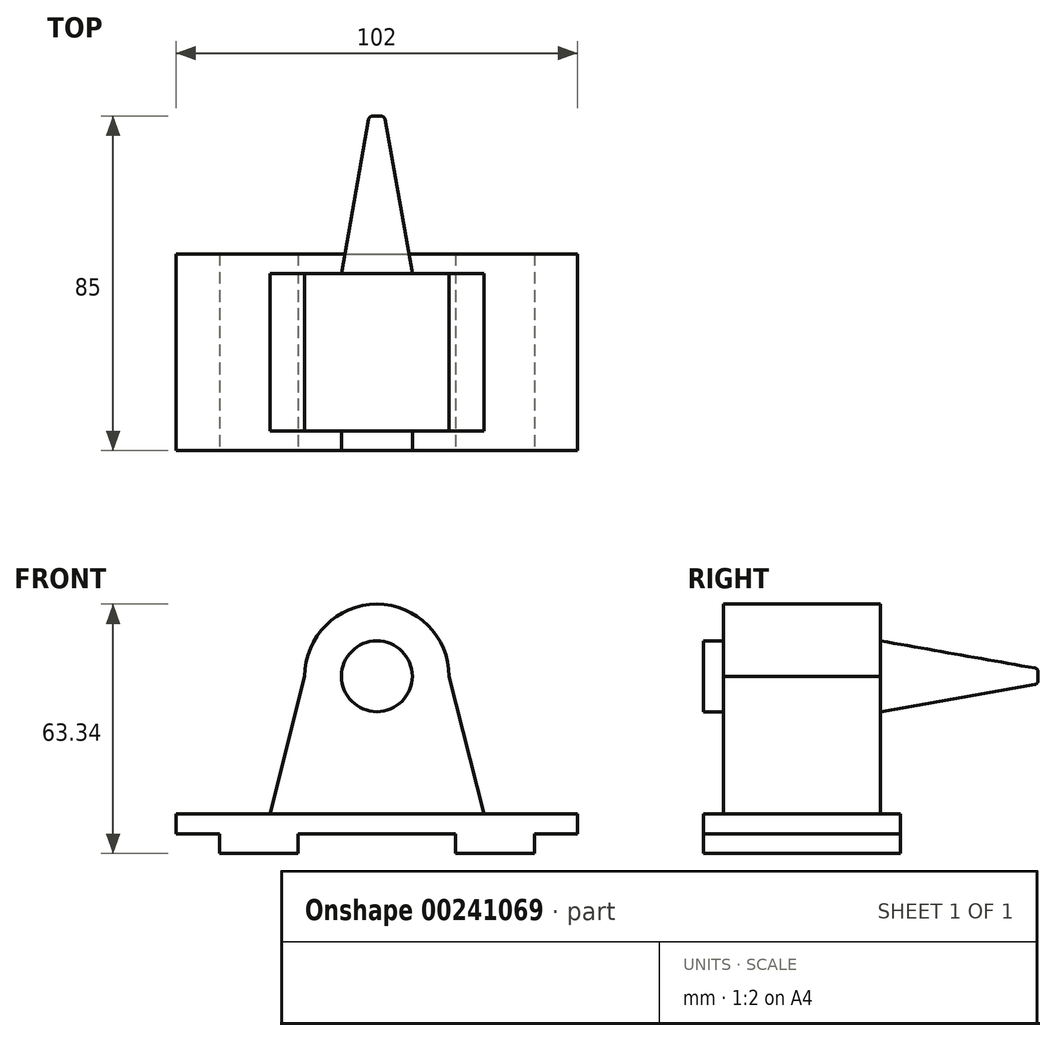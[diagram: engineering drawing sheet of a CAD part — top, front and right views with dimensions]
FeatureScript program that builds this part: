
annotation { "Feature Type Name" : "Feature", "Feature Type Description" : "" }
export const myFeature = defineFeature(function(context is Context, id is Id, definition is map)
    precondition{}
    {
        {
            var Q0;
            Q0=qCreatedBy(makeId("Front.planeOp"),FACE);
            var sketch = newSketch(context, id + "F0", { "sketchPlane" : qUnion([Q0])});
            skLineSegment(sketch, "E0.bottom", {"start": v(2.6, 120.47) * mm, "end": v(22.6, 120.47) * mm});
            skLineSegment(sketch, "E0.top", {"start": v(2.6, 115.47) * mm, "end": v(22.6, 115.47) * mm});
            skLineSegment(sketch, "E0.left", {"start": v(22.6, 120.47) * mm, "end": v(22.6, 115.47) * mm});
            skLineSegment(sketch, "E0.right", {"start": v(2.6, 120.47) * mm, "end": v(2.6, 115.47) * mm});
            skLineSegment(sketch, "E1.bottom", {"start": v(-8.4, 125.47) * mm, "end": v(93.6, 125.47) * mm});
            skLineSegment(sketch, "E1.top", {"start": v(-8.4, 120.47) * mm, "end": v(93.6, 120.47) * mm});
            skLineSegment(sketch, "E1.left", {"start": v(-8.4, 125.47) * mm, "end": v(-8.4, 120.47) * mm});
            skLineSegment(sketch, "E1.right", {"start": v(93.6, 125.47) * mm, "end": v(93.6, 120.47) * mm});
            skLineSegment(sketch, "E2", {"start": v(42.6, 203.58) * mm, "end": v(42.6, 216.68) * mm, "construction": true});
            skPoint(sketch, "E2.startSnap0", {"position": v(42.6, 125.47) * mm});
            skLineSegment(sketch, "E3.MirrorCS", {"start": v(62.6, 120.47) * mm, "end": v(62.6, 115.47) * mm});
            skLineSegment(sketch, "E4.MirrorCS", {"start": v(82.6, 120.47) * mm, "end": v(82.6, 115.47) * mm});
            skLineSegment(sketch, "E5.MirrorCS", {"start": v(82.6, 115.47) * mm, "end": v(62.6, 115.47) * mm});
            skLineSegment(sketch, "E6", {"start": v(15.42, 125.47) * mm, "end": v(24.27, 160.47) * mm});
            skLineSegment(sketch, "E7.MirrorCS", {"start": v(69.8, 125.47) * mm, "end": v(60.94, 160.47) * mm});
            skArc(sketch, "E8", {"start": v(24.27, 160.47) * mm, "mid": v(42.6, 178.81) * mm, "end": v(60.94, 160.47) * mm});
            skCircle(sketch, "E9", {"center": v(42.6, 160.47) * mm, "radius": 9 * mm});
            skSolve(sketch);
        }
        {
            var Q0;
            Q0=makeQuery(id+"F0.imprint","IMPRINT",FACE,{"disambiguationData":[TD([[makeQuery(id+"F0.imprint","IMPRINT",EDGE,{"derivedFrom":sQuery(id+"F0.wireOp",EDGE,"E1.bottom")}),-1.0]])]});
            var Q1;
            Q1=makeQuery(id+"F0.imprint","IMPRINT",FACE,{"disambiguationData":[TD([[makeQuery(id+"F0.imprint","IMPRINT",EDGE,{"derivedFrom":sQuery(id+"F0.wireOp",EDGE,"E0.top")}),1.0]])]});
            var Q2;
            {var subQ0=sQuery(id+"F0.wireOp",EDGE,"E3.MirrorCS");Q2=makeQuery(id+"F0.imprint","IMPRINT",FACE,{"disambiguationData":[TD([[makeQuery(id+"F0.imprint","IMPRINT",EDGE,{"derivedFrom":subQ0}),1.0]])]});}
            extrude(context, id + "F1", {"entities" : qUnion([Q0, Q1, Q2]), "oppositeDirection" : true, "depth" : 50 * mm});
        }
        {
            var Q0;
            {var subQ1=sQuery(id+"F0.wireOp",EDGE,"E6");Q0=makeQuery(id+"F0.imprint","IMPRINT",FACE,{"disambiguationData":[TD([[makeQuery(id+"F0.imprint","IMPRINT",EDGE,{"derivedFrom":subQ1}),-1.0]])]});}
            extrude(context, id + "F2", {"entities" : qUnion([Q0]), "operationType" : NewBodyOperationType.ADD, "oppositeDirection" : true, "depth" : 45 * mm, "hasSecondDirection" : true, "secondDirectionOppositeDirection" : true, "secondDirectionDepth" : 5 * mm});
        }
        {
            var Q0;
            Q0=makeQuery(id+"F0.imprint","IMPRINT",FACE,{"disambiguationData":[TD([[makeQuery(id+"F0.imprint","IMPRINT",EDGE,{"derivedFrom":sQuery(id+"F0.wireOp",EDGE,"E9")}),1.0]])]});
            var Q1;
            Q1=makeQuery(id+"F2.opExtrude","CAP_FACE",FACE,{"disambiguationData":[OSD([sQuery(id+"F0.wireOp",EDGE,"E1.bottom"),sQuery(id+"F0.wireOp",EDGE,"E6"),sQuery(id+"F0.wireOp",EDGE,"E7.MirrorCS"),sQuery(id+"F0.wireOp",EDGE,"E8"),sQuery(id+"F0.wireOp",EDGE,"E9")])],"isStart":false});
            var Q2;
            Q2=makeQuery(id+"F2.opExtrude","CAP_VERTEX",VERTEX,{"disambiguationData":[OSD([sQuery(id+"F0.wireOp",EDGE,"E1.bottom"),sQuery(id+"F0.wireOp",EDGE,"E7.MirrorCS")])],"isStart":false});
            extrude(context, id + "F3", {"entities" : qUnion([Q0]), "endBound" : BoundingType.UP_TO_SURFACE, "oppositeDirection" : true, "endBoundEntityFace" : qUnion([Q1]), "endBoundEntityVertex" : qUnion([Q2]), "depth" : 25 * mm});
        }
        {
            var Q0;
            Q0=makeQuery(id+"F3.opExtrude","CAP_FACE",FACE,{"disambiguationData":[OSD([sQuery(id+"F0.wireOp",EDGE,"E1.bottom"),sQuery(id+"F0.wireOp",EDGE,"E6"),sQuery(id+"F0.wireOp",EDGE,"E7.MirrorCS"),sQuery(id+"F0.wireOp",EDGE,"E8"),sQuery(id+"F0.wireOp",EDGE,"E9")])],"isStart":false});
            extrude(context, id + "F4", {"entities" : qUnion([Q0]), "operationType" : NewBodyOperationType.ADD, "depth" : 40 * mm, "hasDraft" : true, "draftAngle" : 10 * degree, "draftPullDirection" : true});
        }
        {
            var Q0;
            Q0=makeQuery(id+"F4.opExtrude","CAP_EDGE",EDGE,{"disambiguationData":[OSD([sQuery(id+"F0.wireOp",EDGE,"E1.bottom"),sQuery(id+"F0.wireOp",EDGE,"E6"),sQuery(id+"F0.wireOp",EDGE,"E7.MirrorCS"),sQuery(id+"F0.wireOp",EDGE,"E8"),sQuery(id+"F0.wireOp",EDGE,"E9")])],"isStart":false});
            fillet(context, id + "F5", {"entities" : qUnion([Q0]), "radius" : 1 * mm, "tangentPropagation" : true, "allowEdgeOverflow" : false});
        }
    });
